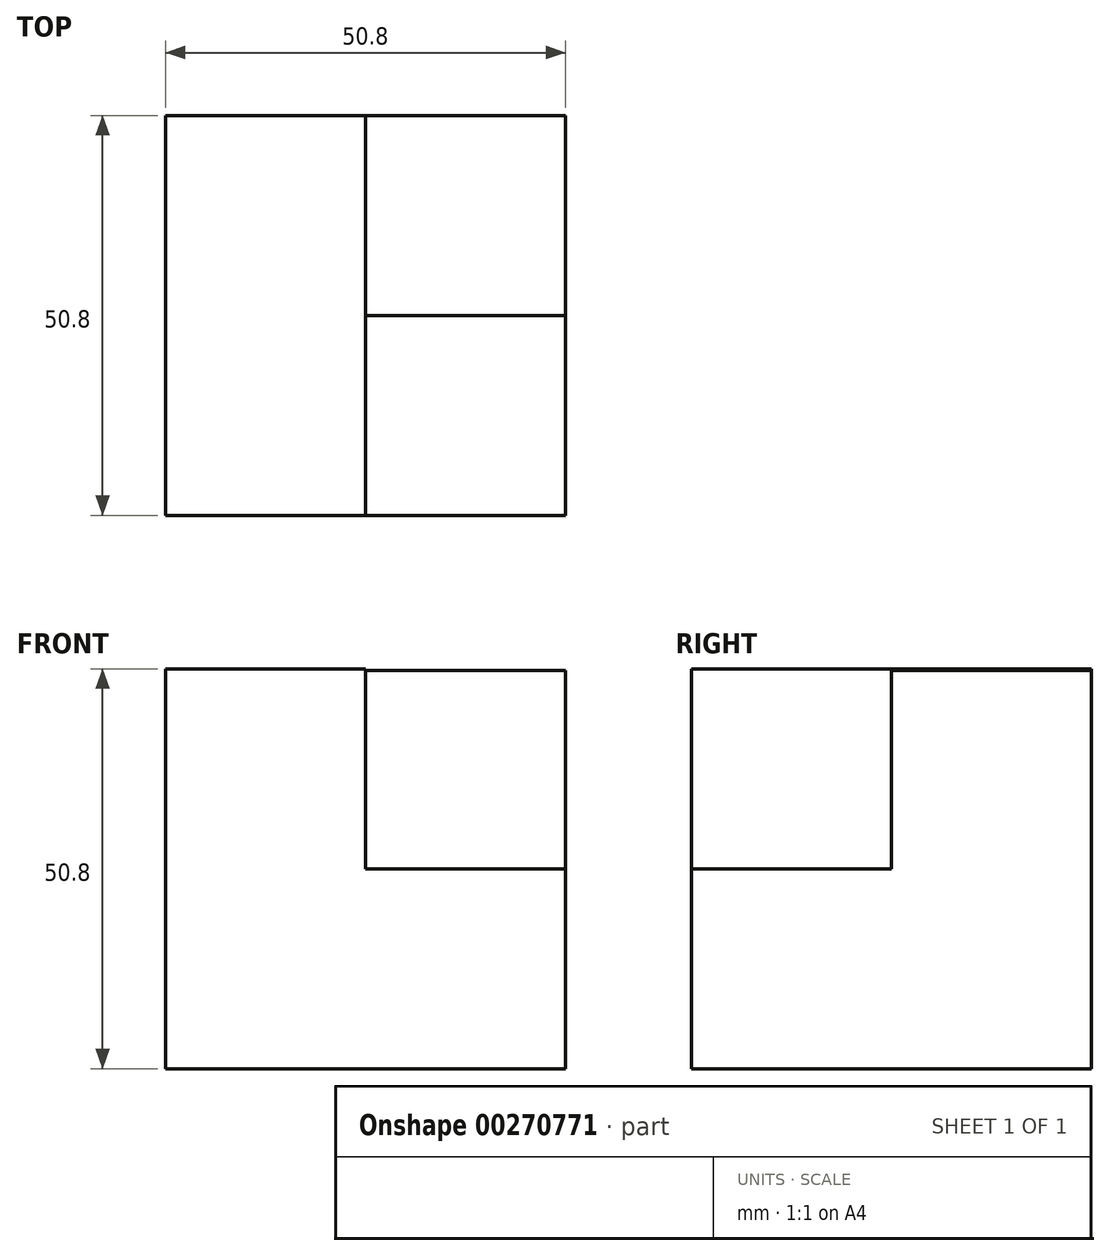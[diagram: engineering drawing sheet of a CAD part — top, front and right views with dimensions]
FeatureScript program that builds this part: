
annotation { "Feature Type Name" : "Feature", "Feature Type Description" : "" }
export const myFeature = defineFeature(function(context is Context, id is Id, definition is map)
    precondition{}
    {
        {
            var Q0;
            Q0=qCreatedBy(makeId("Front.planeOp"),FACE);
            var sketch = newSketch(context, id + "F0", { "sketchPlane" : qUnion([Q0])});
            skLineSegment(sketch, "E0", {"start": v(0, 0) * mm, "end": v(-50.8, 0) * mm});
            skLineSegment(sketch, "E1", {"start": v(-50.8, 0) * mm, "end": v(-50.8, 50.8) * mm});
            skLineSegment(sketch, "E2", {"start": v(-50.8, 50.8) * mm, "end": v(-25.4, 50.8) * mm});
            skLineSegment(sketch, "E3", {"start": v(-25.4, 50.8) * mm, "end": v(-25.4, 25.4) * mm});
            skLineSegment(sketch, "E4", {"start": v(-25.4, 25.4) * mm, "end": v(0, 25.4) * mm});
            skLineSegment(sketch, "E5", {"start": v(0, 25.4) * mm, "end": v(0, 0) * mm});
            skSolve(sketch);
        }
        {
            var Q0;
            Q0 = qSketchRegion(id + "F0", true);
            extrude(context, id + "F1", {"entities" : qUnion([Q0]), "depth" : 50.8 * mm});
        }
        {
            var Q0;
            Q0=qCreatedBy(makeId("Front.planeOp"),FACE);
            var sketch = newSketch(context, id + "F2", { "sketchPlane" : qUnion([Q0])});
            skLineSegment(sketch, "E6.bottom", {"start": v(-25.4, 50.6) * mm, "end": v(0, 50.6) * mm});
            skLineSegment(sketch, "E6.top", {"start": v(-25.4, 25.2) * mm, "end": v(0, 25.2) * mm});
            skLineSegment(sketch, "E6.left", {"start": v(-25.4, 50.6) * mm, "end": v(-25.4, 25.2) * mm});
            skLineSegment(sketch, "E6.right", {"start": v(0, 50.6) * mm, "end": v(0, 25.2) * mm});
            skSolve(sketch);
        }
        {
            var Q0;
            Q0 = qSketchRegion(id + "F2", true);
            extrude(context, id + "F3", {"entities" : qUnion([Q0]), "operationType" : NewBodyOperationType.ADD, "depth" : 25.4 * mm});
        }
    });
